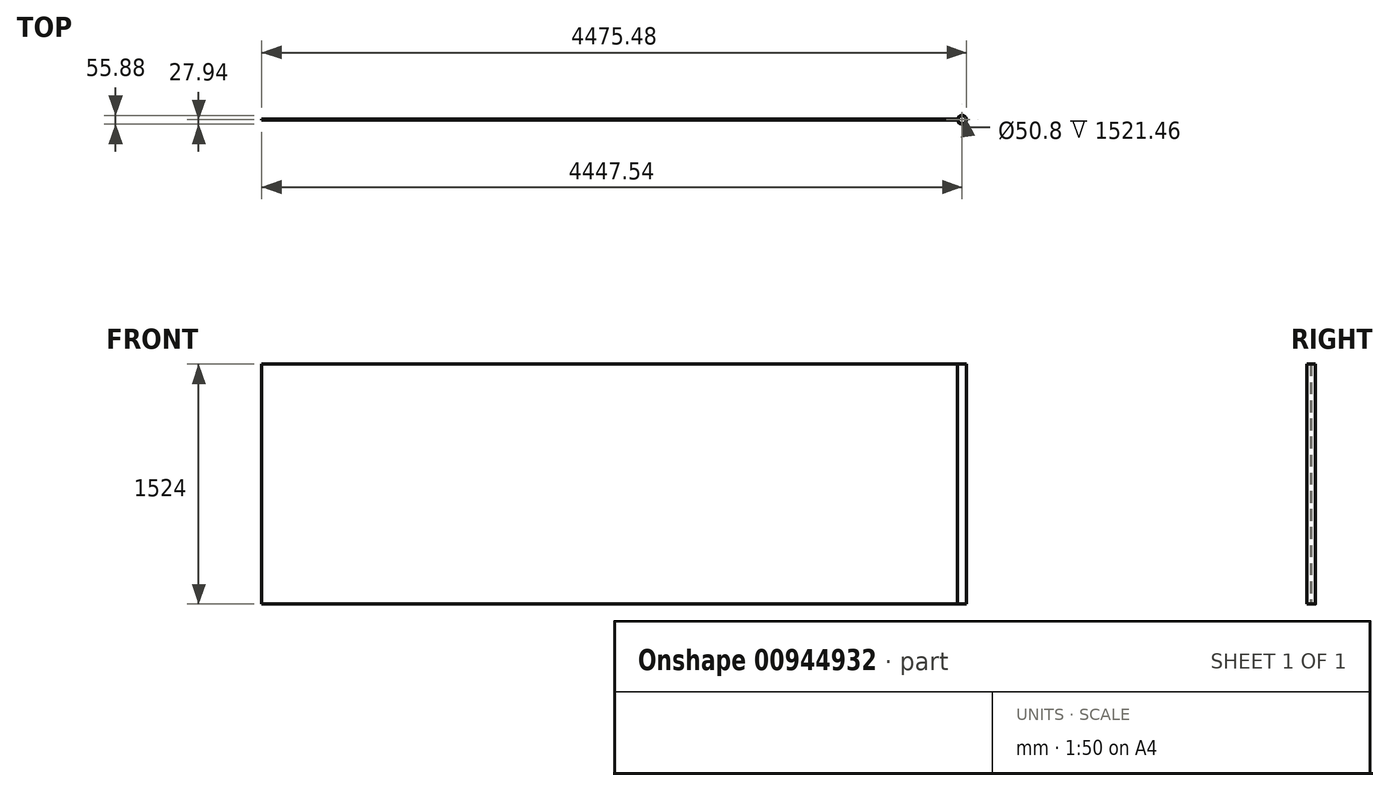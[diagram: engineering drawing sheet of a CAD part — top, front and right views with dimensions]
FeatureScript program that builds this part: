
annotation { "Feature Type Name" : "Feature", "Feature Type Description" : "" }
export const myFeature = defineFeature(function(context is Context, id is Id, definition is map)
    precondition{}
    {
        {
            var Q0;
            Q0=qCreatedBy(makeId("Top.planeOp"),FACE);
            var sketch = newSketch(context, id + "F0", { "sketchPlane" : qUnion([Q0])});
            skLineSegment(sketch, "E0.bottom", {"start": v(2209.8, 3.18) * mm, "end": v(-2209.8, 3.18) * mm});
            skLineSegment(sketch, "E0.top", {"start": v(2209.8, -3.17) * mm, "end": v(-2209.8, -3.17) * mm});
            skLineSegment(sketch, "E0.left", {"start": v(2209.8, 3.18) * mm, "end": v(2209.8, -3.17) * mm});
            skLineSegment(sketch, "E0.right", {"start": v(-2209.8, 3.18) * mm, "end": v(-2209.8, -3.17) * mm});
            skPoint(sketch, "E0.middle", {"position": v(0, 0) * mm});
            skCircle(sketch, "E1", {"center": v(2237.74, 0) * mm, "radius": 27.94 * mm});
            skSolve(sketch);
        }
        {
            var Q0;
            Q0=makeQuery(id+"F0.imprint","IMPRINT",FACE,{"disambiguationData":[TD([[makeQuery(id+"F0.imprint","IMPRINT",EDGE,{"derivedFrom":sQuery(id+"F0.wireOp",EDGE,"E1")}),1.0]])]});
            var Q1;
            {var subQ3=sQuery(id+"F0.wireOp",EDGE,"E0.bottom");Q1=makeQuery(id+"F0.imprint","IMPRINT",FACE,{"disambiguationData":[TD([[makeQuery(id+"F0.imprint","IMPRINT",EDGE,{"derivedFrom":subQ3}),1.0]])]});}
            extrude(context, id + "F1", {"entities" : qUnion([Q0, Q1]), "depth" : 1524 * mm, "offsetDistance" : 25.4 * mm});
        }
        {
            var Q0;
            Q0=makeQuery(id+"F1.opExtrude","CAP_FACE",FACE,{"disambiguationData":[OSD([sQuery(id+"F0.wireOp",EDGE,"E1")])],"isStart":false});
            shell(context, id + "F2", {"entities" : qUnion([Q0]), "thickness" : 2.54 * mm});
        }
    });
